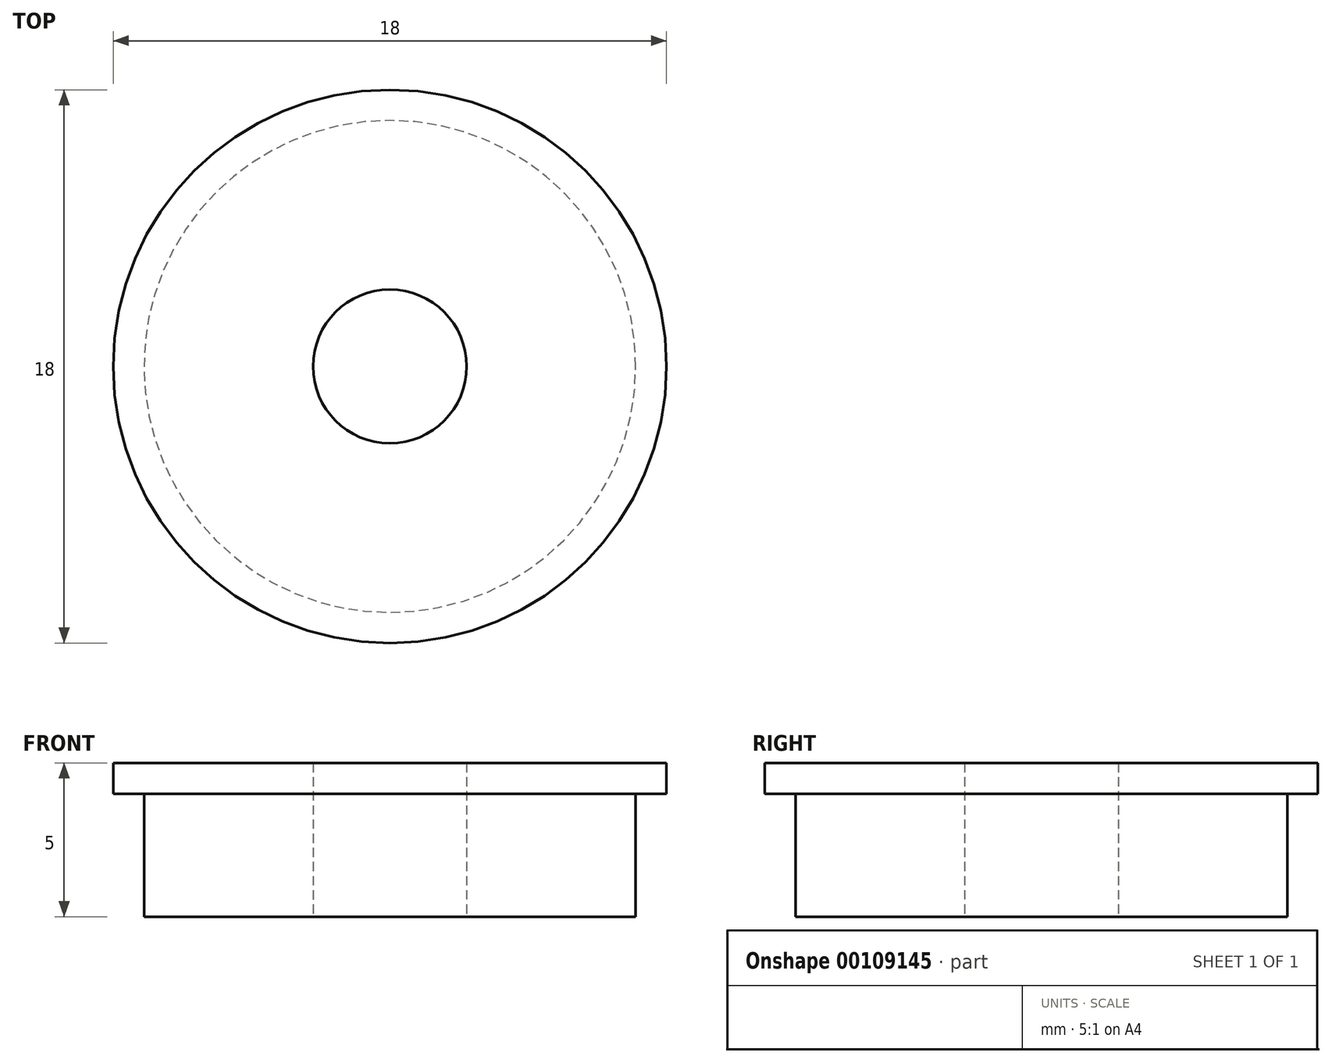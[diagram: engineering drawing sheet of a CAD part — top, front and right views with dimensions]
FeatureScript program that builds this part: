
annotation { "Feature Type Name" : "Feature", "Feature Type Description" : "" }
export const myFeature = defineFeature(function(context is Context, id is Id, definition is map)
    precondition{}
    {
        {
            var Q0;
            Q0=qCreatedBy(makeId("Right.planeOp"),FACE);
            var sketch = newSketch(context, id + "F0", { "sketchPlane" : qUnion([Q0])});
            skLineSegment(sketch, "E0", {"start": v(0, 0) * mm, "end": v(0, 9.32) * mm, "construction": true});
            skLineSegment(sketch, "E1", {"start": v(2.5, 0) * mm, "end": v(2.5, 5) * mm});
            skLineSegment(sketch, "E2", {"start": v(2.5, 5) * mm, "end": v(9, 5) * mm});
            skLineSegment(sketch, "E3", {"start": v(9, 5) * mm, "end": v(9, 4) * mm});
            skLineSegment(sketch, "E4", {"start": v(9, 4) * mm, "end": v(8, 4) * mm});
            skLineSegment(sketch, "E5", {"start": v(8, 4) * mm, "end": v(8, 0) * mm});
            skLineSegment(sketch, "E6", {"start": v(8, 0) * mm, "end": v(2.5, 0) * mm});
            skLineSegment(sketch, "E7", {"start": v(0, 0) * mm, "end": v(2.5, 0) * mm, "construction": true});
            skSolve(sketch);
        }
        {
            var Q0;
            Q0=qSketchRegion(id+"F0",true);
            var Q1;
            Q1=sQuery(id+"F0.wireOp",EDGE,"E0");
            revolve(context, id + "F1", {"entities" : qUnion([Q0]), "axis" : qUnion([Q1]), "revolveType" : RevolveType.FULL});
        }
    });
